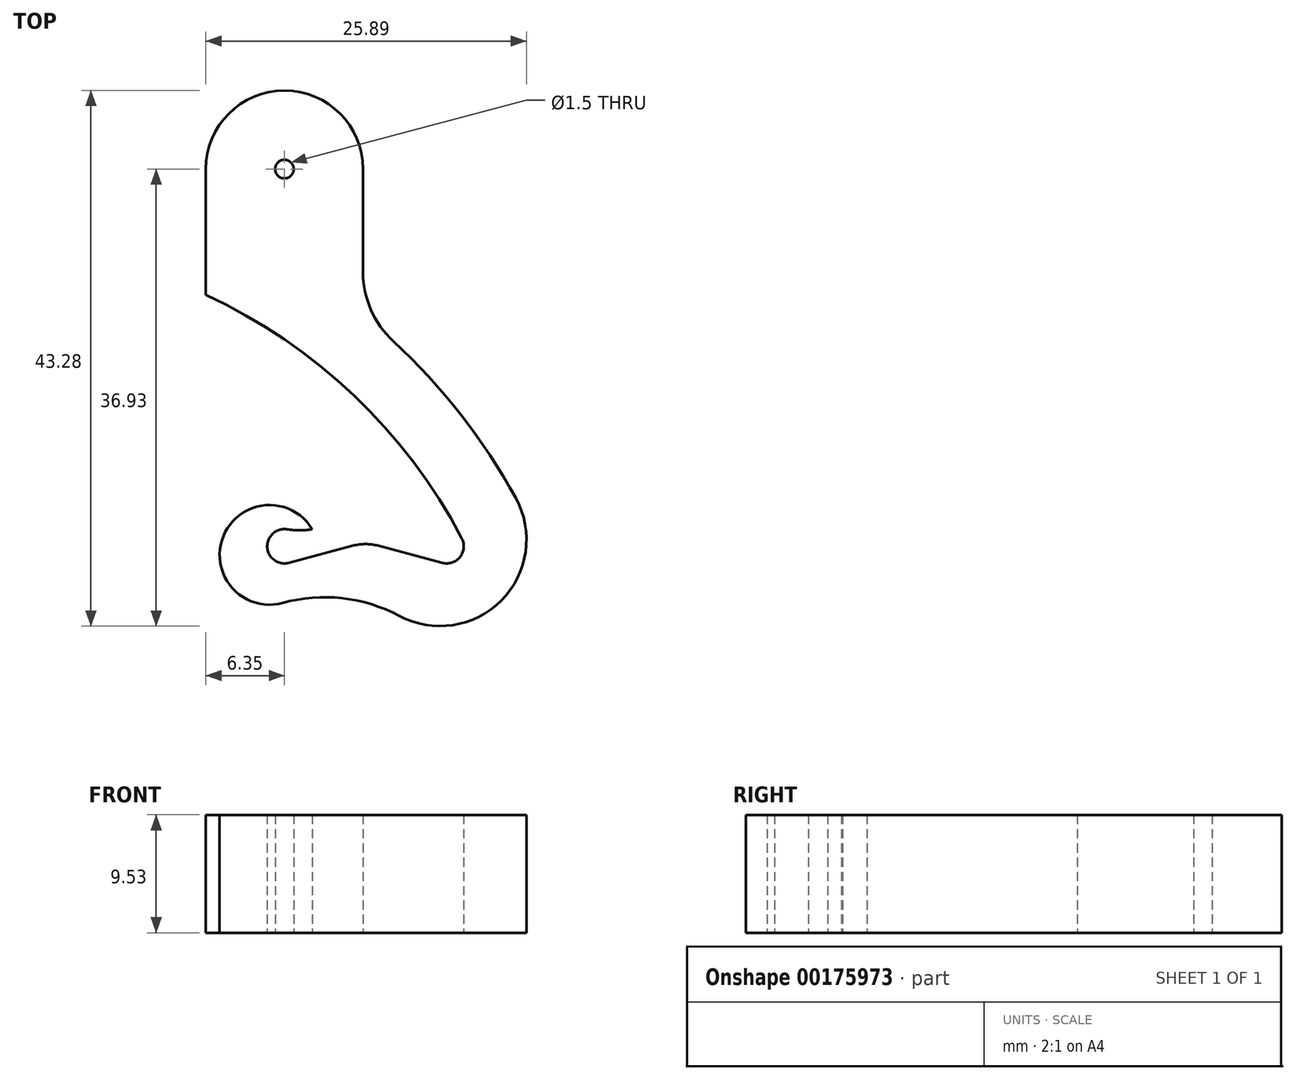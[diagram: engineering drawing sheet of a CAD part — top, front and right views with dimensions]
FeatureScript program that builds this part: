
annotation { "Feature Type Name" : "Feature", "Feature Type Description" : "" }
export const myFeature = defineFeature(function(context is Context, id is Id, definition is map)
    precondition{}
    {
        {
            var Q0;
            Q0=qCreatedBy(makeId("Top.planeOp"),FACE);
            var sketch = newSketch(context, id + "F0", { "sketchPlane" : qUnion([Q0])});
            skArc(sketch, "E0", {"start": v(14.33, 0.65) * mm, "mid": v(5.61, 12.19) * mm, "end": v(-6.35, 20.32) * mm});
            skArc(sketch, "E1", {"start": v(0.22, 1.37) * mm, "mid": v(-1.39, -0.07) * mm, "end": v(0.36, -1.34) * mm});
            skLineSegment(sketch, "E2", {"start": v(0.36, -1.34) * mm, "end": v(5.56, 0.05) * mm});
            skArc(sketch, "E3", {"start": v(12.74, -1.34) * mm, "mid": v(14.18, -0.87) * mm, "end": v(14.33, 0.65) * mm});
            skArc(sketch, "E4", {"start": v(7.53, 0.05) * mm, "mid": v(6.55, 0.18) * mm, "end": v(5.56, 0.05) * mm});
            skLineSegment(sketch, "E5", {"start": v(7.53, 0.05) * mm, "end": v(12.74, -1.34) * mm});
            skLineSegment(sketch, "E6", {"start": v(-6.35, 20.32) * mm, "end": v(-6.35, 30.48) * mm});
            skLineSegment(sketch, "E7", {"start": v(6.35, 30.48) * mm, "end": v(6.35, 22.16) * mm});
            skArc(sketch, "E8", {"start": v(6.35, 22.16) * mm, "mid": v(6.99, 19.11) * mm, "end": v(8.8, 16.57) * mm});
            skLineSegment(sketch, "E9", {"start": v(0, 0) * mm, "end": v(-1.39, 0) * mm, "construction": true});
            skLineSegment(sketch, "E10", {"start": v(0, 0) * mm, "end": v(-1.2, -0.7) * mm, "construction": true});
            skArc(sketch, "E11", {"start": v(9.26, -5.62) * mm, "mid": v(4.67, -4.2) * mm, "end": v(-0.13, -4.58) * mm});
            skArc(sketch, "E12", {"start": v(0.22, 1.37) * mm, "mid": v(1.24, 1.29) * mm, "end": v(2.25, 1.37) * mm});
            skLineSegment(sketch, "E13", {"start": v(2.25, 1.37) * mm, "end": v(0.22, 1.37) * mm, "construction": true});
            skPoint(sketch, "E14", {"position": v(0, 30.48) * mm});
            skLineSegment(sketch, "E15", {"start": v(-1.2, -0.7) * mm, "end": v(-5.6, -3.23) * mm, "construction": true});
            skArc(sketch, "E16", {"start": v(2.25, 1.37) * mm, "mid": v(-4.94, 0.8) * mm, "end": v(-0.13, -4.58) * mm});
            skArc(sketch, "E17", {"start": v(9.26, -5.62) * mm, "mid": v(17.52, -4.38) * mm, "end": v(18.69, 3.89) * mm});
            skLineSegment(sketch, "E18", {"start": v(13.1, 0) * mm, "end": v(12.56, 0.54) * mm, "construction": true});
            skLineSegment(sketch, "E19", {"start": v(13.1, 0) * mm, "end": v(11.25, 0) * mm, "construction": true});
            skArc(sketch, "E20", {"start": v(8.8, 16.57) * mm, "mid": v(14.26, 10.63) * mm, "end": v(18.69, 3.89) * mm});
            skArc(sketch, "E21", {"start": v(6.35, 30.48) * mm, "mid": v(0, 36.83) * mm, "end": v(-6.35, 30.48) * mm});
            skCircle(sketch, "E22", {"center": v(0, 30.48) * mm, "radius": 0.75 * mm});
            skSolve(sketch);
        }
        {
            var Q0;
            Q0 = qSketchRegion(id + "F0", true);
            extrude(context, id + "F1", {"entities" : qUnion([Q0]), "depth" : 9.52 * mm});
        }
    });
